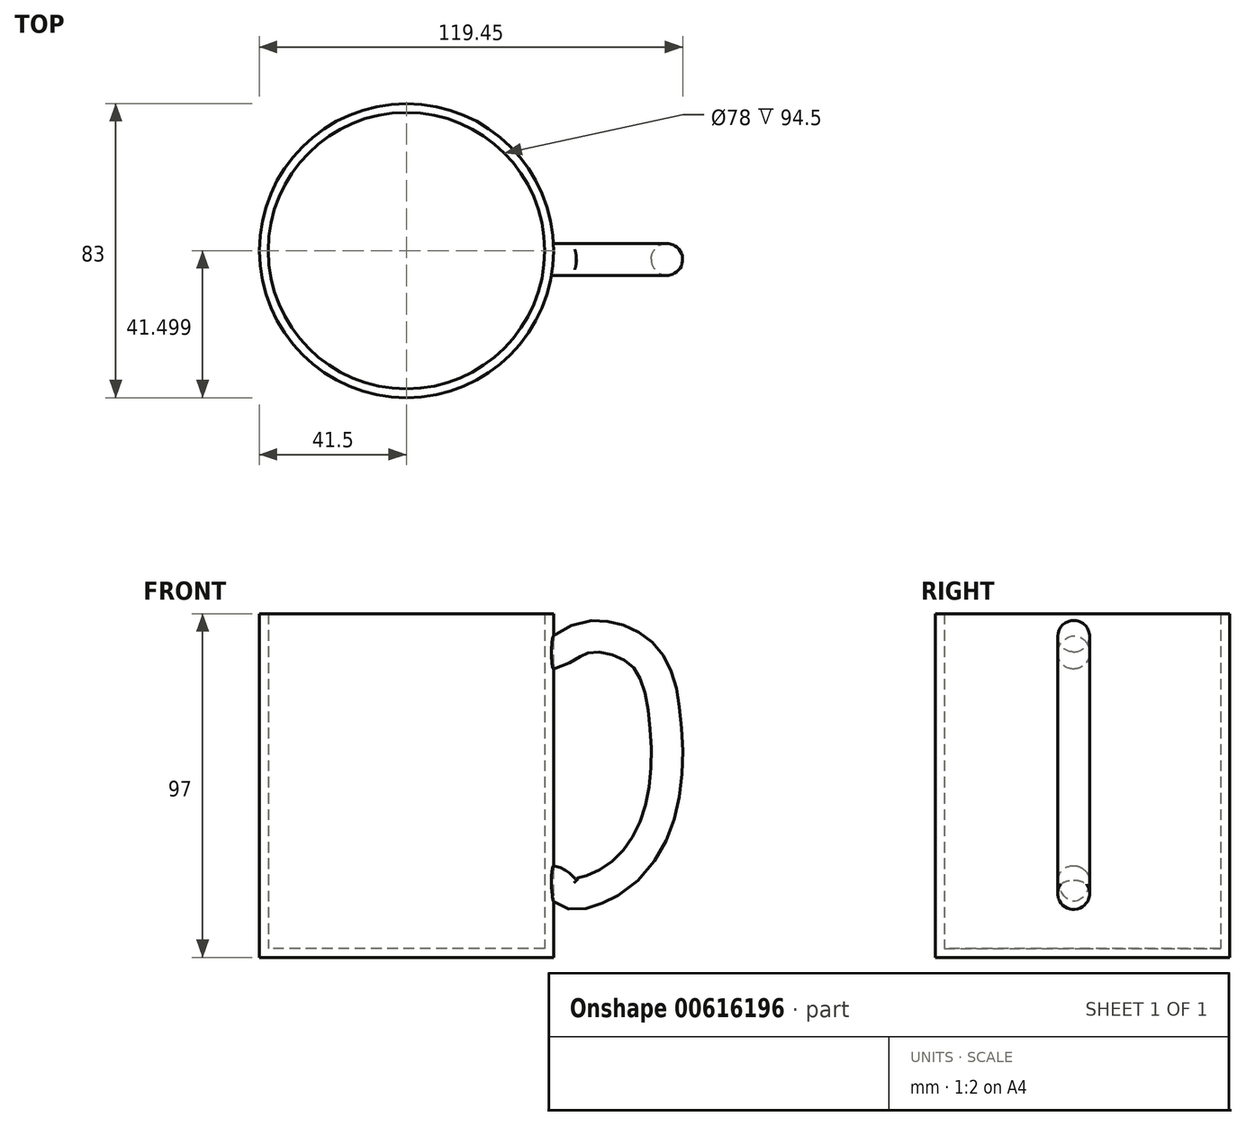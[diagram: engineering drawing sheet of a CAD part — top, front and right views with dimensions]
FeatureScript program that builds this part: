
annotation { "Feature Type Name" : "Feature", "Feature Type Description" : "" }
export const myFeature = defineFeature(function(context is Context, id is Id, definition is map)
    precondition{}
    {
        {
            var Q0;
            Q0=qCreatedBy(makeId("Top.planeOp"),FACE);
            var sketch = newSketch(context, id + "F0", { "sketchPlane" : qUnion([Q0])});
            skCircle(sketch, "E0", {"center": v(0, 2.48) * mm, "radius": 41.5 * mm});
            skSolve(sketch);
        }
        {
            var Q0;
            Q0 = qSketchRegion(id + "F0", true);
            extrude(context, id + "F1", {"entities" : qUnion([Q0]), "depth" : 97 * mm, "offsetDistance" : 25 * mm});
        }
        {
            var Q0;
            Q0=qCreatedBy(makeId("Front.planeOp"),FACE);
            var sketch = newSketch(context, id + "F2", { "sketchPlane" : qUnion([Q0])});
            skFitSpline(sketch, "E1", {"points": [v(39.63, 85.41) * mm, v(50.33, 90.1) * mm, v(66.05, 85.75) * mm, v(72.74, 67.69) * mm, v(71.4, 41.27) * mm, v(59.03, 22.54) * mm, v(45.65, 18.53) * mm, v(38.63, 21.87) * mm], "startDerivative": vector(114.62, 16.37) * mm, "endDerivative": vector(-152.45, 0) * mm});
            skSolve(sketch);
        }
        {
            var Q0;
            Q0=qCreatedBy(makeId("Right.planeOp"),FACE);
            cPlane(context, id + "F3", {"entities" : qUnion([Q0]), "cplaneType" : CPlaneType.OFFSET, "offset" : 40 * mm, "width" : 150 * mm, "height" : 150 * mm});
        }
        {
            var Q0;
            Q0=qCreatedBy(id+"F3.planeOp",FACE);
            var sketch = newSketch(context, id + "F4", { "sketchPlane" : qUnion([Q0])});
            skCircle(sketch, "E2", {"center": v(0, 85.66) * mm, "radius": 4.5 * mm});
            skSolve(sketch);
        }
        {
            var Q0;
            Q0 = qSketchRegion(id + "F4", true);
            var Q1;
            Q1 = qConstructionFilter(qBodyType(qCreatedBy(id + "F2" ,EDGE), BodyType.WIRE), ConstructionObject.NO);
            sweep(context, id + "F5", {"operationType" : NewBodyOperationType.ADD, "profiles" : qUnion([Q0]), "path" : qUnion([Q1])});
        }
        {
            var Q0;
            Q0=makeQuery(id+"F1.opExtrude","CAP_FACE",FACE,{"disambiguationData":[OSD([sQuery(id+"F0.wireOp",EDGE,"E0")])],"isStart":false});
            shell(context, id + "F6", {"entities" : qUnion([Q0]), "thickness" : 2.5 * mm});
        }
    });
